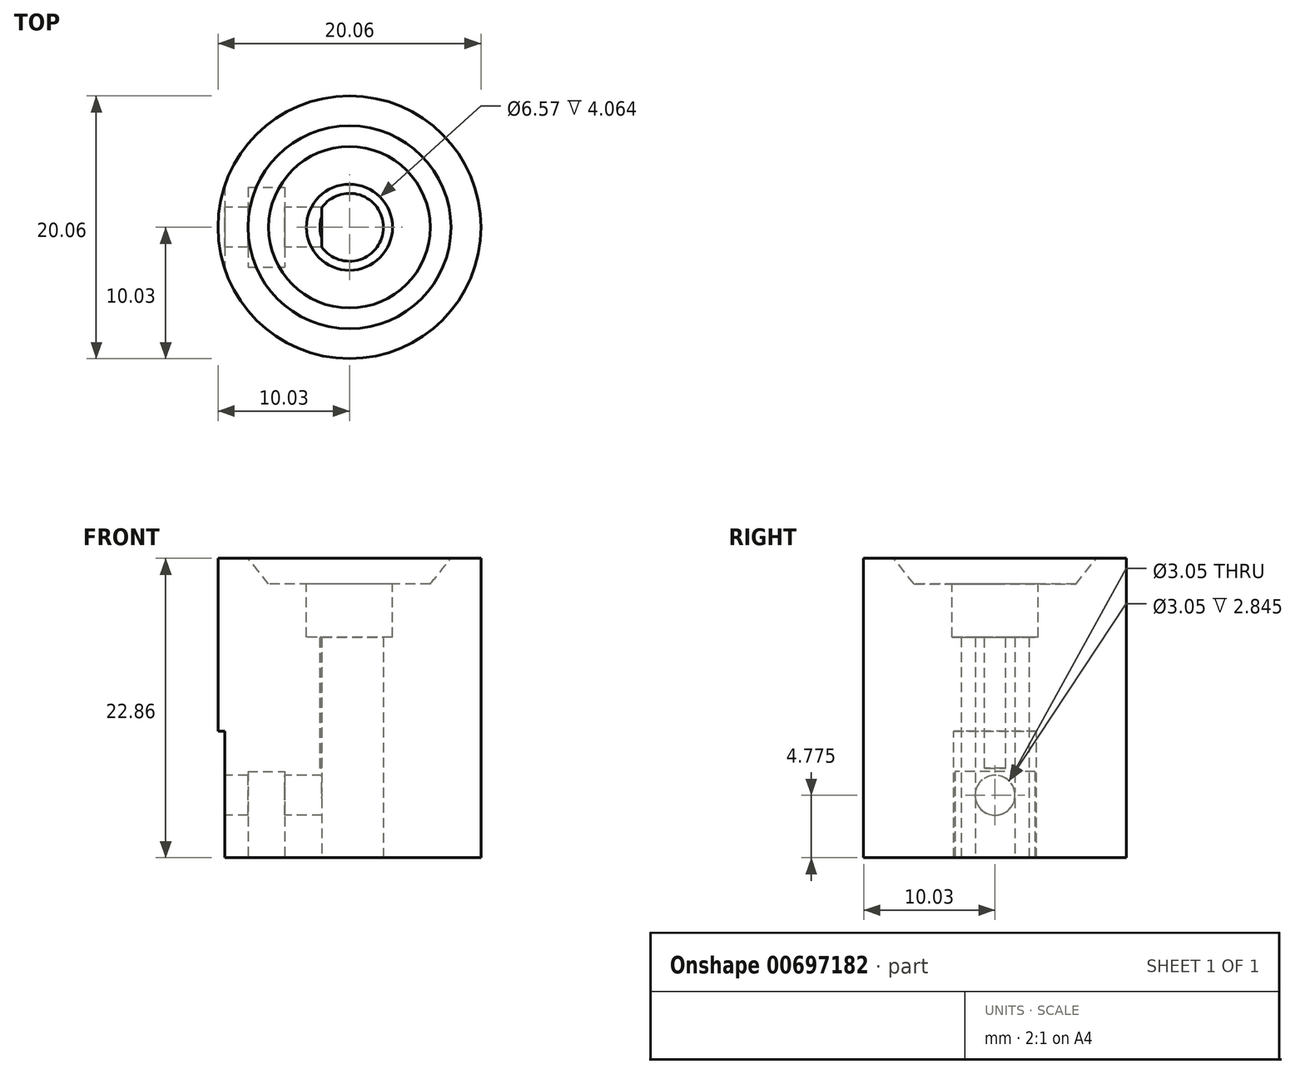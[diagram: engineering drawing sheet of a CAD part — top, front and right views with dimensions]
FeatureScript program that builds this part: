
annotation { "Feature Type Name" : "Feature", "Feature Type Description" : "" }
export const myFeature = defineFeature(function(context is Context, id is Id, definition is map)
    precondition{}
    {
        {
            var Q0;
            Q0=qCreatedBy(makeId("Front.planeOp"),FACE);
            var sketch = newSketch(context, id + "F0", { "sketchPlane" : qUnion([Q0])});
            skLineSegment(sketch, "E0", {"start": v(0, 0) * mm, "end": v(10.03, 0) * mm});
            skLineSegment(sketch, "E1", {"start": v(10.03, 0) * mm, "end": v(10.03, 22.86) * mm});
            skLineSegment(sketch, "E2", {"start": v(10.03, 22.86) * mm, "end": v(7.75, 22.86) * mm});
            skLineSegment(sketch, "E3", {"start": v(2.05, 6.85) * mm, "end": v(0, 6.85) * mm});
            skLineSegment(sketch, "E4", {"start": v(0, 6.85) * mm, "end": v(0, 0) * mm});
            skLineSegment(sketch, "E5", {"start": v(3.29, 20.9) * mm, "end": v(6.16, 20.9) * mm});
            skLineSegment(sketch, "E6", {"start": v(6.16, 20.9) * mm, "end": v(7.75, 22.86) * mm});
            skLineSegment(sketch, "E7", {"start": v(3.29, 20.9) * mm, "end": v(3.29, 16.84) * mm});
            skLineSegment(sketch, "E8", {"start": v(2.25, 16.84) * mm, "end": v(2.25, 6.85) * mm});
            skLineSegment(sketch, "E9", {"start": v(2.25, 16.84) * mm, "end": v(3.29, 16.84) * mm});
            skLineSegment(sketch, "E10", {"start": v(2.25, 6.85) * mm, "end": v(2.05, 6.85) * mm});
            skLineSegment(sketch, "E11", {"start": v(0, 62.98) * mm, "end": v(0, -46.8) * mm, "construction": true});
            skSolve(sketch);
        }
        {
            var Q0;
            Q0 = qSketchRegion(id + "F0", true);
            var Q1;
            Q1=sQuery(id+"F0.wireOp",EDGE,"E11");
            revolve(context, id + "F1", {"entities" : qUnion([Q0]), "axis" : qUnion([Q1]), "revolveType" : RevolveType.FULL});
        }
        {
            var Q0;
            Q0=makeQuery(id+"F1.opRevolve","SWEPT_FACE",FACE,{"disambiguationData":[OSD([sQuery(id+"F0.wireOp",EDGE,"E0")])]});
            var sketch = newSketch(context, id + "F2", { "sketchPlane" : qUnion([Q0])});
            skArc(sketch, "E12", {"start": v(-2.1, 1.5) * mm, "mid": v(2.6, 0) * mm, "end": v(-2.1, -1.5) * mm});
            skLineSegment(sketch, "E13", {"start": v(-2.1, 1.5) * mm, "end": v(-2.1, -1.5) * mm});
            skPoint(sketch, "E14", {"position": v(-10.03, 0) * mm});
            skSolve(sketch);
        }
        {
            var Q0;
            Q0 = qSketchRegion(id + "F2", true);
            extrude(context, id + "F3", {"entities" : qUnion([Q0]), "operationType" : NewBodyOperationType.REMOVE, "endBound" : BoundingType.THROUGH_ALL, "oppositeDirection" : true, "depth" : 25.4 * mm, "offsetDistance" : 25.4 * mm});
        }
        {
            var Q0;
            Q0=qCreatedBy(makeId("Right.planeOp"),FACE);
            cPlane(context, id + "F4", {"entities" : qUnion([Q0]), "cplaneType" : CPlaneType.OFFSET, "offset" : 10.16 * mm, "oppositeDirection" : true, "width" : 152.4 * mm, "height" : 152.4 * mm});
        }
        {
            var Q0;
            Q0=qCreatedBy(id+"F4.planeOp",FACE);
            var sketch = newSketch(context, id + "F5", { "sketchPlane" : qUnion([Q0])});
            skLineSegment(sketch, "E15.bottom", {"start": v(5.08, 0) * mm, "end": v(-5.08, 0) * mm});
            skLineSegment(sketch, "E15.top", {"start": v(5.08, 9.65) * mm, "end": v(-5.08, 9.65) * mm});
            skLineSegment(sketch, "E15.left", {"start": v(5.08, 0) * mm, "end": v(5.08, 9.65) * mm});
            skLineSegment(sketch, "E15.right", {"start": v(-5.08, 0) * mm, "end": v(-5.08, 9.65) * mm});
            skSolve(sketch);
        }
        {
            var Q0;
            Q0 = qSketchRegion(id + "F5", true);
            extrude(context, id + "F6", {"entities" : qUnion([Q0]), "operationType" : NewBodyOperationType.REMOVE, "depth" : 0.64 * mm, "offsetDistance" : 25.4 * mm});
        }
        {
            var Q0;
            Q0=qCreatedBy(id+"F4.planeOp",FACE);
            var sketch = newSketch(context, id + "F7", { "sketchPlane" : qUnion([Q0])});
            skCircle(sketch, "E16", {"center": v(0, 4.78) * mm, "radius": 1.52 * mm});
            skSolve(sketch);
        }
        {
            var Q0;
            Q0 = qSketchRegion(id + "F7", true);
            var Q1;
            Q1=qCreatedBy(makeId("Right.planeOp"),FACE);
            extrude(context, id + "F8", {"entities" : qUnion([Q0]), "operationType" : NewBodyOperationType.REMOVE, "endBound" : BoundingType.UP_TO_SURFACE, "depth" : 25.4 * mm, "endBoundEntityFace" : qUnion([Q1]), "offsetDistance" : 25.4 * mm});
        }
        {
            var Q0;
            Q0=makeQuery(id+"F1.opRevolve","SWEPT_FACE",FACE,{"disambiguationData":[OSD([sQuery(id+"F0.wireOp",EDGE,"E0")])]});
            var sketch = newSketch(context, id + "F9", { "sketchPlane" : qUnion([Q0])});
            skLineSegment(sketch, "E17.bottom", {"start": v(-7.75, -3.05) * mm, "end": v(-4.95, -3.05) * mm});
            skLineSegment(sketch, "E17.top", {"start": v(-7.75, 3.05) * mm, "end": v(-4.95, 3.05) * mm});
            skLineSegment(sketch, "E17.left", {"start": v(-7.75, -3.05) * mm, "end": v(-7.75, 3.05) * mm});
            skLineSegment(sketch, "E17.right", {"start": v(-4.95, -3.05) * mm, "end": v(-4.95, 3.05) * mm});
            skPoint(sketch, "E18", {"position": v(-4.95, 0) * mm});
            skSolve(sketch);
        }
        {
            var Q0;
            Q0 = qSketchRegion(id + "F9", true);
            extrude(context, id + "F10", {"entities" : qUnion([Q0]), "operationType" : NewBodyOperationType.REMOVE, "oppositeDirection" : true, "depth" : 6.6 * mm, "offsetDistance" : 25.4 * mm});
        }
    });
